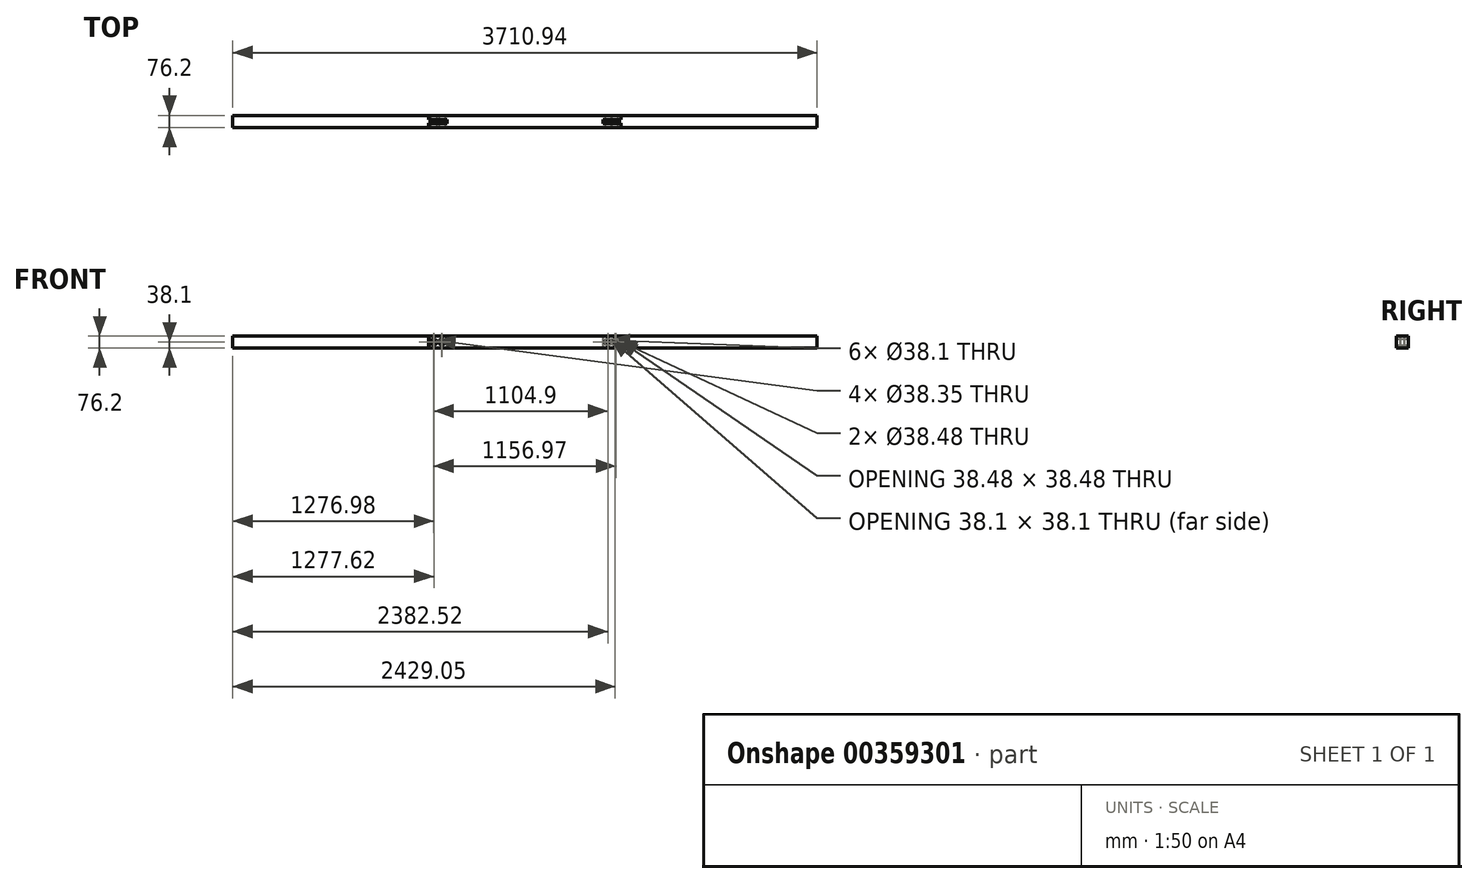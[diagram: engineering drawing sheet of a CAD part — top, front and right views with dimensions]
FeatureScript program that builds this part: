
annotation { "Feature Type Name" : "Feature", "Feature Type Description" : "" }
export const myFeature = defineFeature(function(context is Context, id is Id, definition is map)
    precondition{}
    {
        {
            var Q0;
            Q0=qCreatedBy(makeId("Front.planeOp"),FACE);
            var sketch = newSketch(context, id + "F0", { "sketchPlane" : qUnion([Q0])});
            skLineSegment(sketch, "E0.bottom", {"start": v(609.6, 38.1) * mm, "end": v(-609.6, 38.1) * mm});
            skLineSegment(sketch, "E0.top", {"start": v(609.6, -38.1) * mm, "end": v(-609.6, -38.1) * mm});
            skLineSegment(sketch, "E0.left", {"start": v(609.6, 38.1) * mm, "end": v(609.6, -38.1) * mm});
            skLineSegment(sketch, "E0.right", {"start": v(-609.6, 38.1) * mm, "end": v(-609.6, -38.1) * mm});
            skPoint(sketch, "E0.middle", {"position": v(0, 0) * mm});
            skCircle(sketch, "E1", {"center": v(573.58, 0) * mm, "radius": 19.24 * mm});
            skCircle(sketch, "E2", {"center": v(-577.85, 0) * mm, "radius": 19.05 * mm});
            skSolve(sketch);
        }
        {
            var Q0;
            Q0 = qSketchRegion(id + "F0", true);
            extrude(context, id + "F1", {"entities" : qUnion([Q0]), "depth" : 76.2 * mm});
        }
        {
            var Q0;
            Q0=makeQuery(id+"F1.opExtrude","SWEPT_FACE",FACE,{"disambiguationData":[OSD([sQuery(id+"F0.wireOp",EDGE,"E0.bottom")])]});
            var sketch = newSketch(context, id + "F2", { "sketchPlane" : qUnion([Q0])});
            skLineSegment(sketch, "E3.bottom", {"start": v(-609.6, -50.8) * mm, "end": v(-495.3, -50.8) * mm});
            skLineSegment(sketch, "E3.top", {"start": v(-609.6, -25.4) * mm, "end": v(-495.3, -25.4) * mm});
            skLineSegment(sketch, "E3.left", {"start": v(-609.6, -50.8) * mm, "end": v(-609.6, -25.4) * mm});
            skLineSegment(sketch, "E3.right", {"start": v(-495.3, -50.8) * mm, "end": v(-495.3, -25.4) * mm});
            skSolve(sketch);
        }
        {
            var Q0;
            Q0=makeQuery(id+"F2.imprint","IMPRINT",FACE,{"disambiguationData":[TD([[makeQuery(id+"F2.imprint","IMPRINT",EDGE,{"derivedFrom":sQuery(id+"F2.wireOp",EDGE,"E3.bottom")}),1.0]])]});
            extrude(context, id + "F3", {"entities" : qUnion([Q0]), "operationType" : NewBodyOperationType.REMOVE, "oppositeDirection" : true, "depth" : 76.2 * mm});
        }
        {
            var Q0;
            Q0=makeQuery(id+"F1.opExtrude","SWEPT_FACE",FACE,{"disambiguationData":[OSD([sQuery(id+"F0.wireOp",EDGE,"E0.bottom")])]});
            var sketch = newSketch(context, id + "F4", { "sketchPlane" : qUnion([Q0])});
            skLineSegment(sketch, "E4.bottom", {"start": v(609.6, -50.8) * mm, "end": v(495.3, -50.8) * mm});
            skLineSegment(sketch, "E4.top", {"start": v(609.6, -25.4) * mm, "end": v(495.3, -25.4) * mm});
            skLineSegment(sketch, "E4.left", {"start": v(609.6, -50.8) * mm, "end": v(609.6, -25.4) * mm});
            skLineSegment(sketch, "E4.right", {"start": v(495.3, -50.8) * mm, "end": v(495.3, -25.4) * mm});
            skSolve(sketch);
        }
        {
            var Q0;
            Q0 = qSketchRegion(id + "F4", true);
            extrude(context, id + "F5", {"entities" : qUnion([Q0]), "operationType" : NewBodyOperationType.REMOVE, "oppositeDirection" : true, "depth" : 76.2 * mm});
        }
        {
            var Q0;
            Q0=makeQuery(id+"F1.opExtrude","CAP_FACE",FACE,{"disambiguationData":[OSD([sQuery(id+"F0.wireOp",EDGE,"E0.bottom"),sQuery(id+"F0.wireOp",EDGE,"E0.top"),sQuery(id+"F0.wireOp",EDGE,"E0.left"),sQuery(id+"F0.wireOp",EDGE,"E0.right"),sQuery(id+"F0.wireOp",EDGE,"E1"),sQuery(id+"F0.wireOp",EDGE,"E2")])],"isStart":false});
            var sketch = newSketch(context, id + "F6", { "sketchPlane" : qUnion([Q0])});
            skCircle(sketch, "E5", {"center": v(-527.05, 0) * mm, "radius": 19.05 * mm});
            skCircle(sketch, "E6", {"center": v(527.05, 0) * mm, "radius": 19.05 * mm});
            skSolve(sketch);
        }
        {
            var Q0;
            Q0 = qSketchRegion(id + "F6", true);
            extrude(context, id + "F7", {"entities" : qUnion([Q0]), "operationType" : NewBodyOperationType.REMOVE, "oppositeDirection" : true, "depth" : 76.2 * mm});
        }
        {
            var Q0;
            Q0=qCreatedBy(makeId("Top.planeOp"),FACE);
            var sketch = newSketch(context, id + "F8", { "sketchPlane" : qUnion([Q0])});
            skLineSegment(sketch, "E7", {"start": v(-495.94, -26.03) * mm, "end": v(-495.94, -50.16) * mm});
            skLineSegment(sketch, "E8", {"start": v(-495.94, -50.16) * mm, "end": v(-610.87, -50.16) * mm});
            skLineSegment(sketch, "E9", {"start": v(-610.87, -50.17) * mm, "end": v(-610.87, -76.2) * mm});
            skLineSegment(sketch, "E10", {"start": v(-610.87, -76.2) * mm, "end": v(-636.27, -76.2) * mm});
            skLineSegment(sketch, "E11", {"start": v(-636.27, -76.2) * mm, "end": v(-636.27, 0) * mm});
            skLineSegment(sketch, "E12", {"start": v(-636.27, 0) * mm, "end": v(-610.87, 0) * mm});
            skLineSegment(sketch, "E13", {"start": v(-610.87, 0) * mm, "end": v(-610.87, -26.04) * mm});
            skLineSegment(sketch, "E14", {"start": v(-610.87, -26.04) * mm, "end": v(-495.94, -26.03) * mm});
            skPoint(sketch, "E15.orphan", {"position": v(-495.94, -24.7) * mm});
            skSolve(sketch);
        }
        {
            var Q0;
            Q0 = qSketchRegion(id + "F8", true);
            extrude(context, id + "F9", {"entities" : qUnion([Q0]), "endBound" : BoundingType.SYMMETRIC, "depth" : 76.2 * mm});
        }
        {
            var Q0;
            Q0=makeQuery(id+"F9.opExtrude","SWEPT_FACE",FACE,{"disambiguationData":[OSD([sQuery(id+"F8.wireOp",EDGE,"E14")])]});
            var sketch = newSketch(context, id + "F10", { "sketchPlane" : qUnion([Q0])});
            skCircle(sketch, "E16", {"center": v(578.49, 0) * mm, "radius": 19.18 * mm});
            skCircle(sketch, "E17", {"center": v(527.68, 0) * mm, "radius": 19.18 * mm});
            skSolve(sketch);
        }
        {
            var Q0;
            Q0=makeQuery(id+"F10.imprint","IMPRINT",FACE,{"disambiguationData":[TD([[makeQuery(id+"F10.imprint","IMPRINT",EDGE,{"derivedFrom":sQuery(id+"F10.wireOp",EDGE,"E16")}),1.0]])]});
            var Q1;
            Q1=makeQuery(id+"F10.imprint","IMPRINT",FACE,{"disambiguationData":[TD([[makeQuery(id+"F10.imprint","IMPRINT",EDGE,{"derivedFrom":sQuery(id+"F10.wireOp",EDGE,"E17")}),1.0]])]});
            var Q2;
            Q2=sQuery(id+"F10.wireOp",EDGE,"E16");
            var Q3;
            Q3=sQuery(id+"F10.wireOp",EDGE,"E17");
            extrude(context, id + "F11", {"entities" : qUnion([Q0, Q1]), "operationType" : NewBodyOperationType.REMOVE, "surfaceEntities" : qUnion([Q2, Q3]), "endBound" : BoundingType.UP_TO_NEXT, "oppositeDirection" : true, "depth" : 50.8 * mm});
        }
        {
            var Q0;
            Q0=makeQuery(id+"F9.opExtrude","SWEPT_BODY",BODY,{"disambiguationData":[OSD([sQuery(id+"F8.wireOp",EDGE,"E7"),sQuery(id+"F8.wireOp",EDGE,"E8"),sQuery(id+"F8.wireOp",EDGE,"E9"),sQuery(id+"F8.wireOp",EDGE,"E10"),sQuery(id+"F8.wireOp",EDGE,"E11"),sQuery(id+"F8.wireOp",EDGE,"E12"),sQuery(id+"F8.wireOp",EDGE,"E13"),sQuery(id+"F8.wireOp",EDGE,"E14")])]});
            var Q1;
            Q1=qCreatedBy(makeId("Right.planeOp"),FACE);
            mirror(context, id + "F12", {"entities" : qUnion([Q0]), "mirrorPlane" : qUnion([Q1])});
        }
        {
            var Q0;
            Q0=makeQuery(id+"F12.opPattern","COPY",FACE,{"derivedFrom":makeQuery(id+"F9.opExtrude","SWEPT_FACE",FACE,{"disambiguationData":[OSD([sQuery(id+"F8.wireOp",EDGE,"E11")])]}),"instanceName":"1"});
            extrude(context, id + "F13", {"entities" : qUnion([Q0]), "depth" : 1219.2 * mm});
        }
        {
            var Q0;
            Q0=makeQuery(id+"F13.opExtrude","SWEPT_BODY",BODY,{"disambiguationData":[OSD([sQuery(id+"F8.wireOp",EDGE,"E11")])]});
            var Q1;
            Q1=qCreatedBy(makeId("Right.planeOp"),FACE);
            mirror(context, id + "F14", {"operationType" : NewBodyOperationType.ADD, "entities" : qUnion([Q0]), "mirrorPlane" : qUnion([Q1])});
        }
    });
